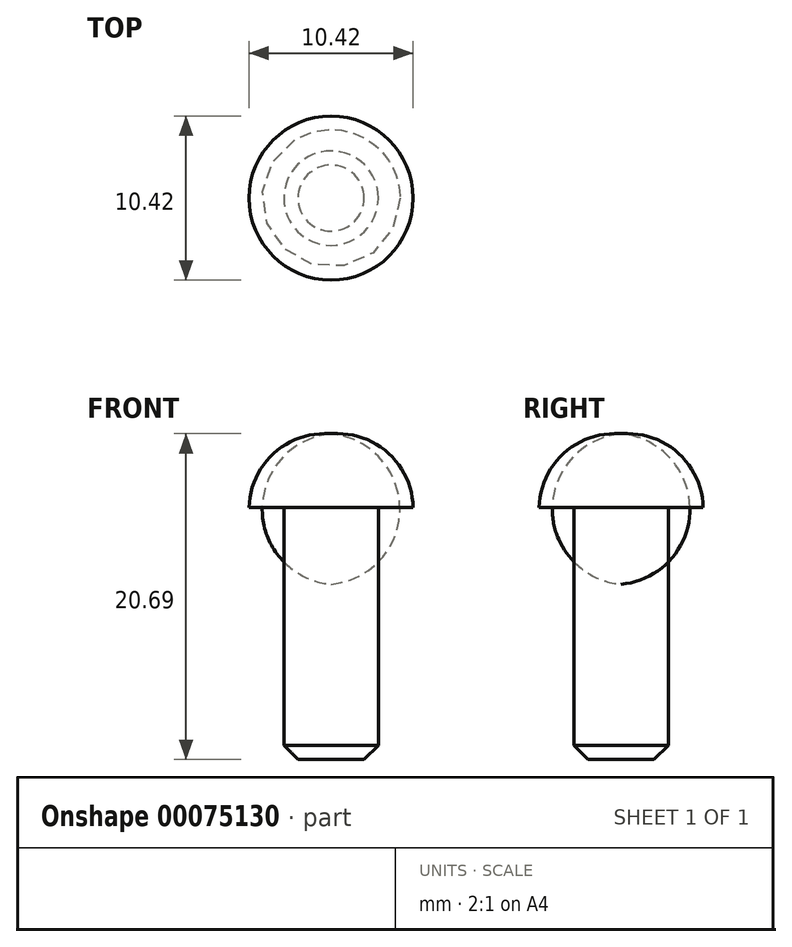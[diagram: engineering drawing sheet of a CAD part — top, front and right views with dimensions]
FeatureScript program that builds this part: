
annotation { "Feature Type Name" : "Feature", "Feature Type Description" : "" }
export const myFeature = defineFeature(function(context is Context, id is Id, definition is map)
    precondition{}
    {
        {
            var Q0;
            Q0=qCreatedBy(makeId("Front.planeOp"),FACE);
            var sketch = newSketch(context, id + "F0", { "sketchPlane" : qUnion([Q0])});
            skLineSegment(sketch, "E0", {"start": v(0, -8.06) * mm, "end": v(2.1, -8.06) * mm});
            skLineSegment(sketch, "E1", {"start": v(2.1, -8.06) * mm, "end": v(3, -7.16) * mm});
            skLineSegment(sketch, "E2", {"start": v(3, -7.16) * mm, "end": v(3, 7.94) * mm});
            skLineSegment(sketch, "E3", {"start": v(0, 7.94) * mm, "end": v(5.2, 7.94) * mm});
            skArc(sketch, "E4", {"start": v(5.2, 7.94) * mm, "mid": v(3.62, 11.4) * mm, "end": v(0, 12.61) * mm});
            skLineSegment(sketch, "E5", {"start": v(0, -8.06) * mm, "end": v(0, 7.94) * mm});
            skLineSegment(sketch, "E6", {"start": v(0, 7.94) * mm, "end": v(0, 12.61) * mm});
            skSolve(sketch);
        }
        {
            var Q0;
            Q0=qSketchRegion(id+"F0",true);
            var Q1;
            Q1=sQuery(id+"F0.wireOp",EDGE,"E5");
            revolve(context, id + "F1", {"entities" : qUnion([Q0]), "axis" : qUnion([Q1]), "revolveType" : RevolveType.FULL});
        }
    });
